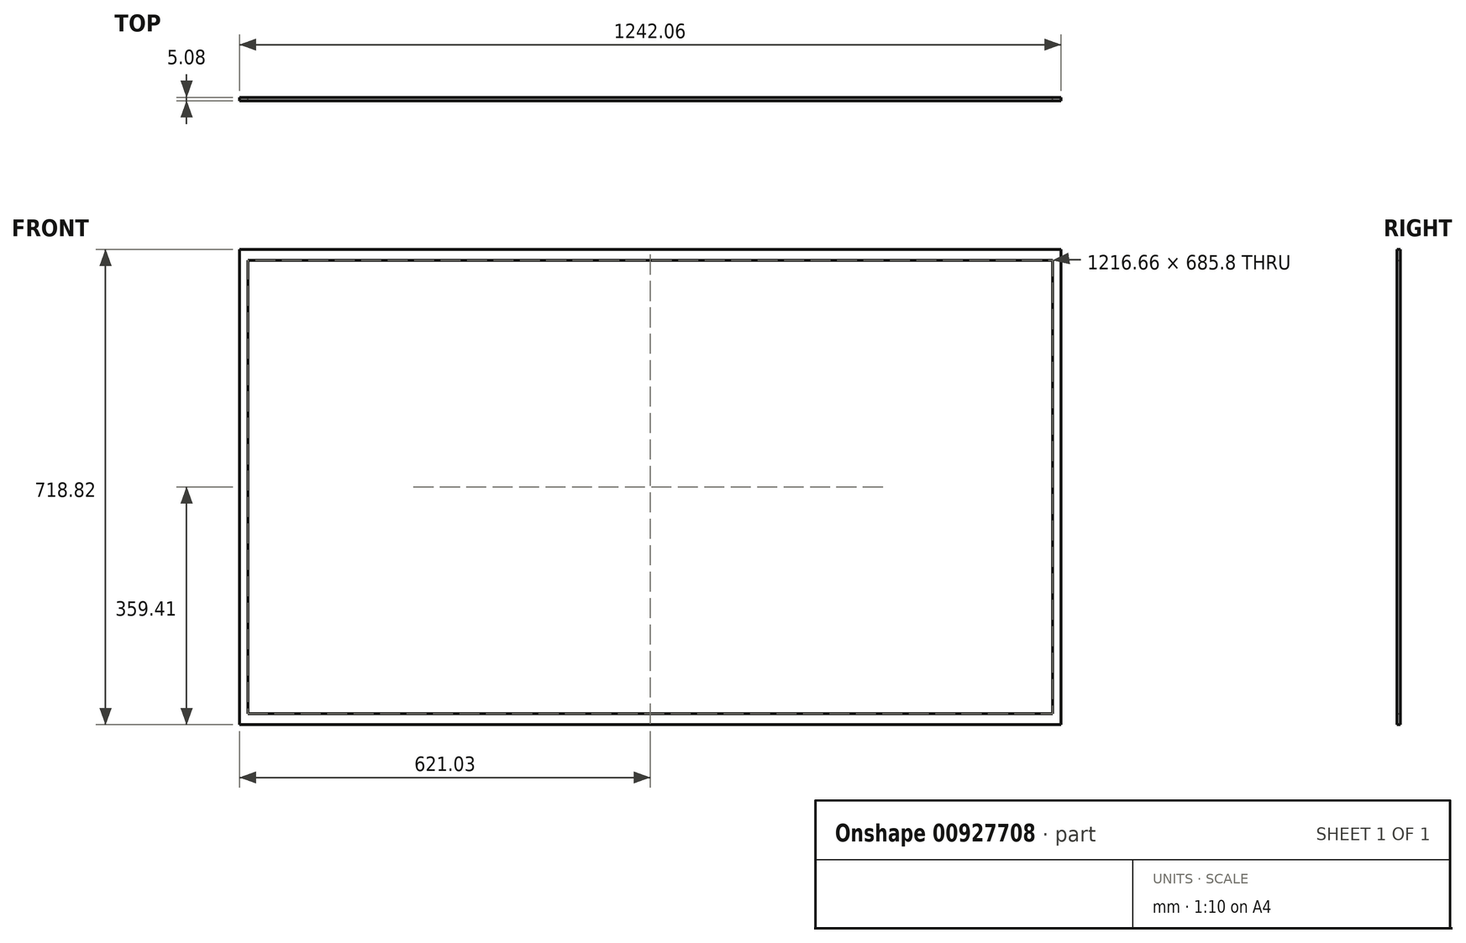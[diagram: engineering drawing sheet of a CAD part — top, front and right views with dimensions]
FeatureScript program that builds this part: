
annotation { "Feature Type Name" : "Feature", "Feature Type Description" : "" }
export const myFeature = defineFeature(function(context is Context, id is Id, definition is map)
    precondition{}
    {
        {
            var Q0;
            Q0=qCreatedBy(makeId("Front.planeOp"),FACE);
            var sketch = newSketch(context, id + "F0", { "sketchPlane" : qUnion([Q0])});
            skLineSegment(sketch, "E0.bottom", {"start": v(-621.03, 0) * mm, "end": v(621.03, 0) * mm});
            skLineSegment(sketch, "E0.top", {"start": v(-621.03, 718.82) * mm, "end": v(621.03, 718.82) * mm});
            skLineSegment(sketch, "E0.left", {"start": v(-621.03, 0) * mm, "end": v(-621.03, 718.82) * mm});
            skLineSegment(sketch, "E0.right", {"start": v(621.03, 0) * mm, "end": v(621.03, 718.82) * mm});
            skLineSegment(sketch, "E1.bottom", {"start": v(-608.33, 702.31) * mm, "end": v(608.33, 702.31) * mm});
            skLineSegment(sketch, "E1.top", {"start": v(-608.33, 16.51) * mm, "end": v(608.33, 16.51) * mm});
            skLineSegment(sketch, "E1.left", {"start": v(-608.33, 702.31) * mm, "end": v(-608.33, 16.51) * mm});
            skLineSegment(sketch, "E1.right", {"start": v(608.33, 702.31) * mm, "end": v(608.33, 16.51) * mm});
            skSolve(sketch);
        }
        {
            var Q0;
            Q0=makeQuery(id+"F0.imprint","IMPRINT",FACE,{"disambiguationData":[TD([[makeQuery(id+"F0.imprint","IMPRINT",EDGE,{"derivedFrom":sQuery(id+"F0.wireOp",EDGE,"E0.bottom")}),1.0]])]});
            var Q1;
            Q1=sQuery(id+"F0.wireOp",EDGE,"E0.top");
            var Q2;
            Q2=sQuery(id+"F0.wireOp",EDGE,"E0.left");
            var Q3;
            Q3=sQuery(id+"F0.wireOp",EDGE,"E0.bottom");
            var Q4;
            Q4=sQuery(id+"F0.wireOp",EDGE,"E1.top");
            var Q5;
            Q5=sQuery(id+"F0.wireOp",EDGE,"E1.right");
            var Q6;
            Q6=sQuery(id+"F0.wireOp",EDGE,"E0.right");
            var Q7;
            Q7=sQuery(id+"F0.wireOp",EDGE,"E1.bottom");
            extrude(context, id + "F1", {"entities" : qUnion([Q0]), "surfaceEntities" : qUnion([Q1, Q2, Q3, Q4, Q5, Q6, Q7]), "depth" : 5.08 * mm, "offsetDistance" : 25.4 * mm});
        }
    });
